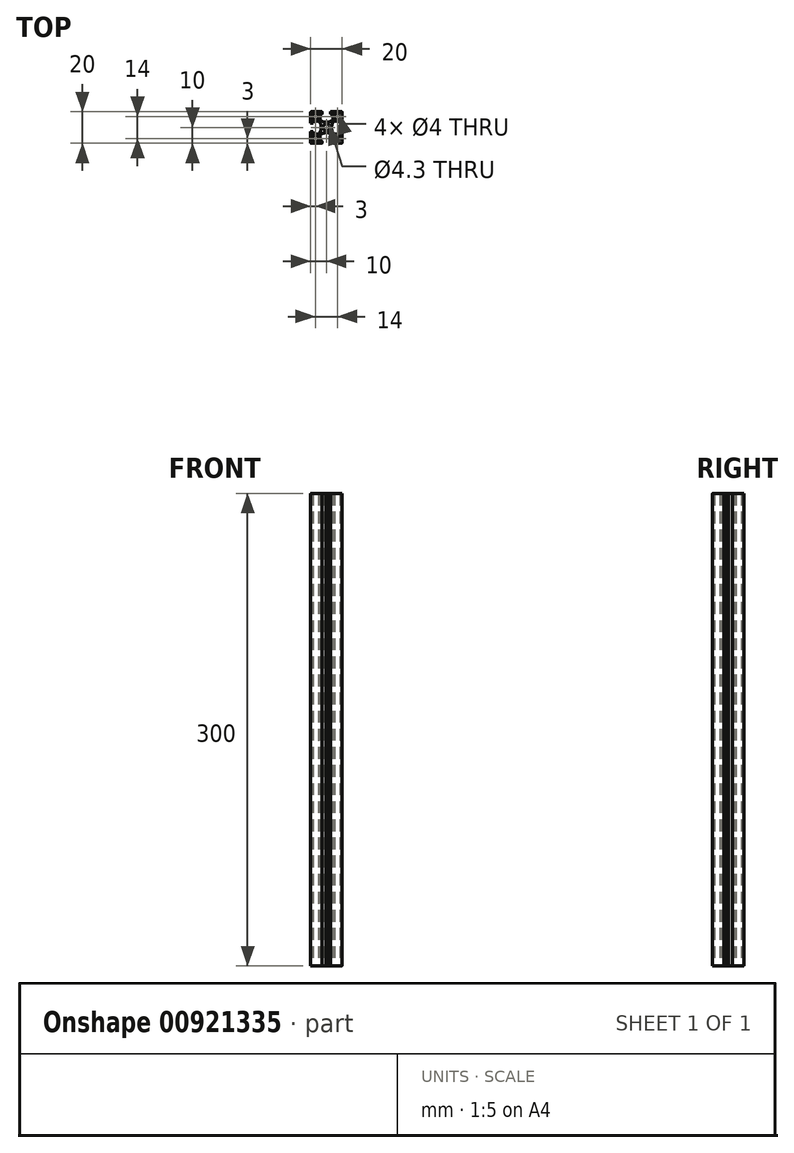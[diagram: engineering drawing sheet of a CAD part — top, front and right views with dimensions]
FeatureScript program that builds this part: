
annotation { "Feature Type Name" : "Feature", "Feature Type Description" : "" }
export const myFeature = defineFeature(function(context is Context, id is Id, definition is map)
    precondition{}
    {
        {
            var Q0;
            Q0=qCreatedBy(makeId("Top.planeOp"),FACE);
            var sketch = newSketch(context, id + "F0", { "sketchPlane" : qUnion([Q0])});
            skLineSegment(sketch, "E0", {"start": v(-11.2, 0) * mm, "end": v(11.2, 0) * mm});
            skCircle(sketch, "E1", {"center": v(0, 0) * mm, "radius": 2.15 * mm});
            skLineSegment(sketch, "E2", {"start": v(4.15, 4.94) * mm, "end": v(4.15, 8.2) * mm});
            skArc(sketch, "E3", {"start": v(4.15, 8.2) * mm, "mid": v(4.06, 8.41) * mm, "end": v(3.85, 8.5) * mm});
            skLineSegment(sketch, "E4", {"start": v(3.85, 8.5) * mm, "end": v(2.95, 8.5) * mm});
            skArc(sketch, "E5", {"start": v(2.95, 8.5) * mm, "mid": v(2.74, 8.59) * mm, "end": v(2.65, 8.8) * mm});
            skLineSegment(sketch, "E6", {"start": v(2.65, 8.8) * mm, "end": v(2.65, 9.7) * mm});
            skArc(sketch, "E7", {"start": v(2.65, 9.7) * mm, "mid": v(2.74, 9.91) * mm, "end": v(2.95, 10) * mm});
            skLineSegment(sketch, "E8", {"start": v(2.95, 10) * mm, "end": v(9.7, 10) * mm});
            skArc(sketch, "E9", {"start": v(9.7, 10) * mm, "mid": v(9.91, 9.91) * mm, "end": v(10, 9.7) * mm});
            skLineSegment(sketch, "E10", {"start": v(10, 9.7) * mm, "end": v(10, 2.95) * mm});
            skArc(sketch, "E11", {"start": v(10, 2.95) * mm, "mid": v(9.91, 2.74) * mm, "end": v(9.7, 2.65) * mm});
            skLineSegment(sketch, "E12", {"start": v(9.7, 2.65) * mm, "end": v(8.8, 2.65) * mm});
            skArc(sketch, "E13", {"start": v(8.8, 2.65) * mm, "mid": v(8.59, 2.74) * mm, "end": v(8.5, 2.95) * mm});
            skLineSegment(sketch, "E14", {"start": v(8.5, 2.95) * mm, "end": v(8.5, 3.85) * mm});
            skArc(sketch, "E15", {"start": v(8.5, 3.85) * mm, "mid": v(8.41, 4.06) * mm, "end": v(8.2, 4.15) * mm});
            skLineSegment(sketch, "E16", {"start": v(8.2, 4.15) * mm, "end": v(4.94, 4.15) * mm});
            skArc(sketch, "E17", {"start": v(4.94, 4.15) * mm, "mid": v(4.81, 4.12) * mm, "end": v(4.7, 4.04) * mm});
            skArc(sketch, "E18", {"start": v(4.7, 4.04) * mm, "mid": v(3.71, 2.28) * mm, "end": v(3.3, 0.3) * mm});
            skLineSegment(sketch, "E19", {"start": v(3.3, 0.3) * mm, "end": v(3, 0) * mm});
            skLineSegment(sketch, "E20", {"start": v(3, 0) * mm, "end": v(3.3, -0.3) * mm});
            skArc(sketch, "E21", {"start": v(3.3, -0.3) * mm, "mid": v(3.71, -2.28) * mm, "end": v(4.7, -4.04) * mm});
            skArc(sketch, "E22", {"start": v(4.7, -4.04) * mm, "mid": v(4.81, -4.12) * mm, "end": v(4.94, -4.15) * mm});
            skLineSegment(sketch, "E23", {"start": v(4.94, -4.15) * mm, "end": v(8.2, -4.15) * mm});
            skArc(sketch, "E24", {"start": v(8.2, -4.15) * mm, "mid": v(8.41, -4.06) * mm, "end": v(8.5, -3.85) * mm});
            skLineSegment(sketch, "E25", {"start": v(8.5, -3.85) * mm, "end": v(8.5, -2.95) * mm});
            skArc(sketch, "E26", {"start": v(8.5, -2.95) * mm, "mid": v(8.59, -2.74) * mm, "end": v(8.8, -2.65) * mm});
            skLineSegment(sketch, "E27", {"start": v(8.8, -2.65) * mm, "end": v(9.7, -2.65) * mm});
            skArc(sketch, "E28", {"start": v(9.7, -2.65) * mm, "mid": v(9.91, -2.74) * mm, "end": v(10, -2.95) * mm});
            skLineSegment(sketch, "E29", {"start": v(10, -2.95) * mm, "end": v(10, -9.7) * mm});
            skArc(sketch, "E30", {"start": v(10, -9.7) * mm, "mid": v(9.91, -9.91) * mm, "end": v(9.7, -10) * mm});
            skLineSegment(sketch, "E31", {"start": v(9.7, -10) * mm, "end": v(2.95, -10) * mm});
            skArc(sketch, "E32", {"start": v(2.95, -10) * mm, "mid": v(2.74, -9.91) * mm, "end": v(2.65, -9.7) * mm});
            skLineSegment(sketch, "E33", {"start": v(2.65, -9.7) * mm, "end": v(2.65, -8.8) * mm});
            skArc(sketch, "E34", {"start": v(2.65, -8.8) * mm, "mid": v(2.74, -8.59) * mm, "end": v(2.95, -8.5) * mm});
            skLineSegment(sketch, "E35", {"start": v(2.95, -8.5) * mm, "end": v(3.85, -8.5) * mm});
            skArc(sketch, "E36", {"start": v(3.85, -8.5) * mm, "mid": v(4.06, -8.41) * mm, "end": v(4.15, -8.2) * mm});
            skLineSegment(sketch, "E37", {"start": v(4.15, -8.2) * mm, "end": v(4.15, -4.94) * mm});
            skArc(sketch, "E38", {"start": v(4.15, -4.94) * mm, "mid": v(4.12, -4.81) * mm, "end": v(4.04, -4.7) * mm});
            skArc(sketch, "E39", {"start": v(4.04, -4.7) * mm, "mid": v(2.28, -3.71) * mm, "end": v(0.3, -3.3) * mm});
            skLineSegment(sketch, "E40", {"start": v(0.3, -3.3) * mm, "end": v(0, -3) * mm});
            skLineSegment(sketch, "E41", {"start": v(0, -3) * mm, "end": v(-0.3, -3.3) * mm});
            skArc(sketch, "E42", {"start": v(-0.3, -3.3) * mm, "mid": v(-2.28, -3.71) * mm, "end": v(-4.04, -4.7) * mm});
            skArc(sketch, "E43", {"start": v(-4.04, -4.7) * mm, "mid": v(-4.12, -4.81) * mm, "end": v(-4.15, -4.94) * mm});
            skLineSegment(sketch, "E44", {"start": v(-4.15, -4.94) * mm, "end": v(-4.15, -8.2) * mm});
            skArc(sketch, "E45", {"start": v(-4.15, -8.2) * mm, "mid": v(-4.06, -8.41) * mm, "end": v(-3.85, -8.5) * mm});
            skLineSegment(sketch, "E46", {"start": v(-3.85, -8.5) * mm, "end": v(-2.95, -8.5) * mm});
            skArc(sketch, "E47", {"start": v(-2.95, -8.5) * mm, "mid": v(-2.74, -8.59) * mm, "end": v(-2.65, -8.8) * mm});
            skLineSegment(sketch, "E48", {"start": v(-2.65, -8.8) * mm, "end": v(-2.65, -9.7) * mm});
            skArc(sketch, "E49", {"start": v(-2.65, -9.7) * mm, "mid": v(-2.74, -9.91) * mm, "end": v(-2.95, -10) * mm});
            skLineSegment(sketch, "E50", {"start": v(-2.95, -10) * mm, "end": v(-9.7, -10) * mm});
            skArc(sketch, "E51", {"start": v(-9.7, -10) * mm, "mid": v(-9.91, -9.91) * mm, "end": v(-10, -9.7) * mm});
            skLineSegment(sketch, "E52", {"start": v(-10, -9.7) * mm, "end": v(-10, -2.95) * mm});
            skArc(sketch, "E53", {"start": v(-10, -2.95) * mm, "mid": v(-9.91, -2.74) * mm, "end": v(-9.7, -2.65) * mm});
            skLineSegment(sketch, "E54", {"start": v(-9.7, -2.65) * mm, "end": v(-8.8, -2.65) * mm});
            skArc(sketch, "E55", {"start": v(-8.8, -2.65) * mm, "mid": v(-8.59, -2.74) * mm, "end": v(-8.5, -2.95) * mm});
            skLineSegment(sketch, "E56", {"start": v(-8.5, -2.95) * mm, "end": v(-8.5, -3.85) * mm});
            skArc(sketch, "E57", {"start": v(-8.5, -3.85) * mm, "mid": v(-8.41, -4.06) * mm, "end": v(-8.2, -4.15) * mm});
            skLineSegment(sketch, "E58", {"start": v(-8.2, -4.15) * mm, "end": v(-4.94, -4.15) * mm});
            skArc(sketch, "E59", {"start": v(-4.94, -4.15) * mm, "mid": v(-4.81, -4.12) * mm, "end": v(-4.7, -4.04) * mm});
            skArc(sketch, "E60", {"start": v(-4.7, -4.04) * mm, "mid": v(-3.71, -2.28) * mm, "end": v(-3.3, -0.3) * mm});
            skLineSegment(sketch, "E61", {"start": v(-3.3, -0.3) * mm, "end": v(-3, 0) * mm});
            skLineSegment(sketch, "E62", {"start": v(-3, 0) * mm, "end": v(-3.3, 0.3) * mm});
            skArc(sketch, "E63", {"start": v(-3.3, 0.3) * mm, "mid": v(-3.71, 2.28) * mm, "end": v(-4.7, 4.04) * mm});
            skArc(sketch, "E64", {"start": v(-4.7, 4.04) * mm, "mid": v(-4.81, 4.12) * mm, "end": v(-4.94, 4.15) * mm});
            skLineSegment(sketch, "E65", {"start": v(-4.94, 4.15) * mm, "end": v(-8.2, 4.15) * mm});
            skArc(sketch, "E66", {"start": v(-8.2, 4.15) * mm, "mid": v(-8.41, 4.06) * mm, "end": v(-8.5, 3.85) * mm});
            skLineSegment(sketch, "E67", {"start": v(-8.5, 3.85) * mm, "end": v(-8.5, 2.95) * mm});
            skArc(sketch, "E68", {"start": v(-8.5, 2.95) * mm, "mid": v(-8.59, 2.74) * mm, "end": v(-8.8, 2.65) * mm});
            skLineSegment(sketch, "E69", {"start": v(-8.8, 2.65) * mm, "end": v(-9.7, 2.65) * mm});
            skArc(sketch, "E70", {"start": v(-9.7, 2.65) * mm, "mid": v(-9.91, 2.74) * mm, "end": v(-10, 2.95) * mm});
            skLineSegment(sketch, "E71", {"start": v(-10, 2.95) * mm, "end": v(-10, 9.7) * mm});
            skArc(sketch, "E72", {"start": v(-10, 9.7) * mm, "mid": v(-9.91, 9.91) * mm, "end": v(-9.7, 10) * mm});
            skLineSegment(sketch, "E73", {"start": v(-9.7, 10) * mm, "end": v(-2.95, 10) * mm});
            skArc(sketch, "E74", {"start": v(-2.95, 10) * mm, "mid": v(-2.74, 9.91) * mm, "end": v(-2.65, 9.7) * mm});
            skLineSegment(sketch, "E75", {"start": v(-2.65, 9.7) * mm, "end": v(-2.65, 8.8) * mm});
            skArc(sketch, "E76", {"start": v(-2.65, 8.8) * mm, "mid": v(-2.74, 8.59) * mm, "end": v(-2.95, 8.5) * mm});
            skLineSegment(sketch, "E77", {"start": v(-2.95, 8.5) * mm, "end": v(-3.85, 8.5) * mm});
            skArc(sketch, "E78", {"start": v(-3.85, 8.5) * mm, "mid": v(-4.06, 8.41) * mm, "end": v(-4.15, 8.2) * mm});
            skLineSegment(sketch, "E79", {"start": v(-4.15, 8.2) * mm, "end": v(-4.15, 4.94) * mm});
            skArc(sketch, "E80", {"start": v(-4.15, 4.94) * mm, "mid": v(-4.12, 4.81) * mm, "end": v(-4.04, 4.7) * mm});
            skArc(sketch, "E81", {"start": v(-4.04, 4.7) * mm, "mid": v(-2.28, 3.71) * mm, "end": v(-0.3, 3.3) * mm});
            skLineSegment(sketch, "E82", {"start": v(-0.3, 3.3) * mm, "end": v(0, 3) * mm});
            skLineSegment(sketch, "E83", {"start": v(0, 3) * mm, "end": v(0.3, 3.3) * mm});
            skArc(sketch, "E84", {"start": v(0.3, 3.3) * mm, "mid": v(2.28, 3.71) * mm, "end": v(4.04, 4.7) * mm});
            skArc(sketch, "E85", {"start": v(4.04, 4.7) * mm, "mid": v(4.12, 4.81) * mm, "end": v(4.15, 4.94) * mm});
            skLineSegment(sketch, "E86", {"start": v(-9.5, 7) * mm, "end": v(-4.5, 7) * mm});
            skLineSegment(sketch, "E87", {"start": v(-7, 9.5) * mm, "end": v(-7, 4.5) * mm});
            skCircle(sketch, "E88", {"center": v(-7, 7) * mm, "radius": 2 * mm});
            skLineSegment(sketch, "E89", {"start": v(-9.5, -7) * mm, "end": v(-4.5, -7) * mm});
            skLineSegment(sketch, "E90", {"start": v(-7, -9.5) * mm, "end": v(-7, -4.5) * mm});
            skCircle(sketch, "E91", {"center": v(-7, -7) * mm, "radius": 2 * mm});
            skLineSegment(sketch, "E92", {"start": v(0, 11.2) * mm, "end": v(0, -11.2) * mm});
            skLineSegment(sketch, "E93", {"start": v(9.5, 7) * mm, "end": v(4.5, 7) * mm});
            skLineSegment(sketch, "E94", {"start": v(7, 9.5) * mm, "end": v(7, 4.5) * mm});
            skCircle(sketch, "E95", {"center": v(7, 7) * mm, "radius": 2 * mm});
            skCircle(sketch, "E96", {"center": v(7, -7) * mm, "radius": 2 * mm});
            skLineSegment(sketch, "E97", {"start": v(7, -9.5) * mm, "end": v(7, -4.5) * mm});
            skLineSegment(sketch, "E98", {"start": v(9.5, -7) * mm, "end": v(4.5, -7) * mm});
            skSolve(sketch);
        }
        {
            var Q0;
            Q0 = qSketchRegion(id + "F0", true);
            extrude(context, id + "F1", {"entities" : qUnion([Q0]), "depth" : 300 * mm, "offsetDistance" : 25 * mm});
        }
    });
